SOLIDWORKS PART (.sldprt)
format: sldprt  version: not decoded by parser v0  size: 286,720 bytes
history: native  units: mm
features: sketch x4, plane x3, extrude x3, material x1, cut_extrude x1, mirror x1, pattern_circular x1 (+13 scaffold rows collapsed)
feature tree (27):
  scaffold x13  (default folders/planes/origin — collapsed)
  material  "材质 <未指定>"
  plane  "前视基准面"
  plane  "上视基准面"
  plane  "右视基准面"
  sketch  "草图1"  dims[D1=100.0mm D2=150.0mm]
  extrude  "凸台-拉伸1"  Depth=100mm
  sketch  "草图2"  dims[D1=1000.0mm D2=1050.0mm]
  extrude  "凸台-拉伸2"  Depth=100mm
  sketch  "草图3"  dims[D1=100.0mm D2=5.0]
  extrude  "凸台-拉伸4"  Depth=50mm
  sketch  "草图4"
  cut_extrude  "切除-拉伸1"  Depth=10mm
  mirror  "镜向1"
  pattern_circular  "阵列(圆周)1"  Count=5 Angle=360deg
decode coverage: 8 of 10 modeling features carry decoded parameters
note: suppression state not decoded; provenance and decode notes live in map.json
